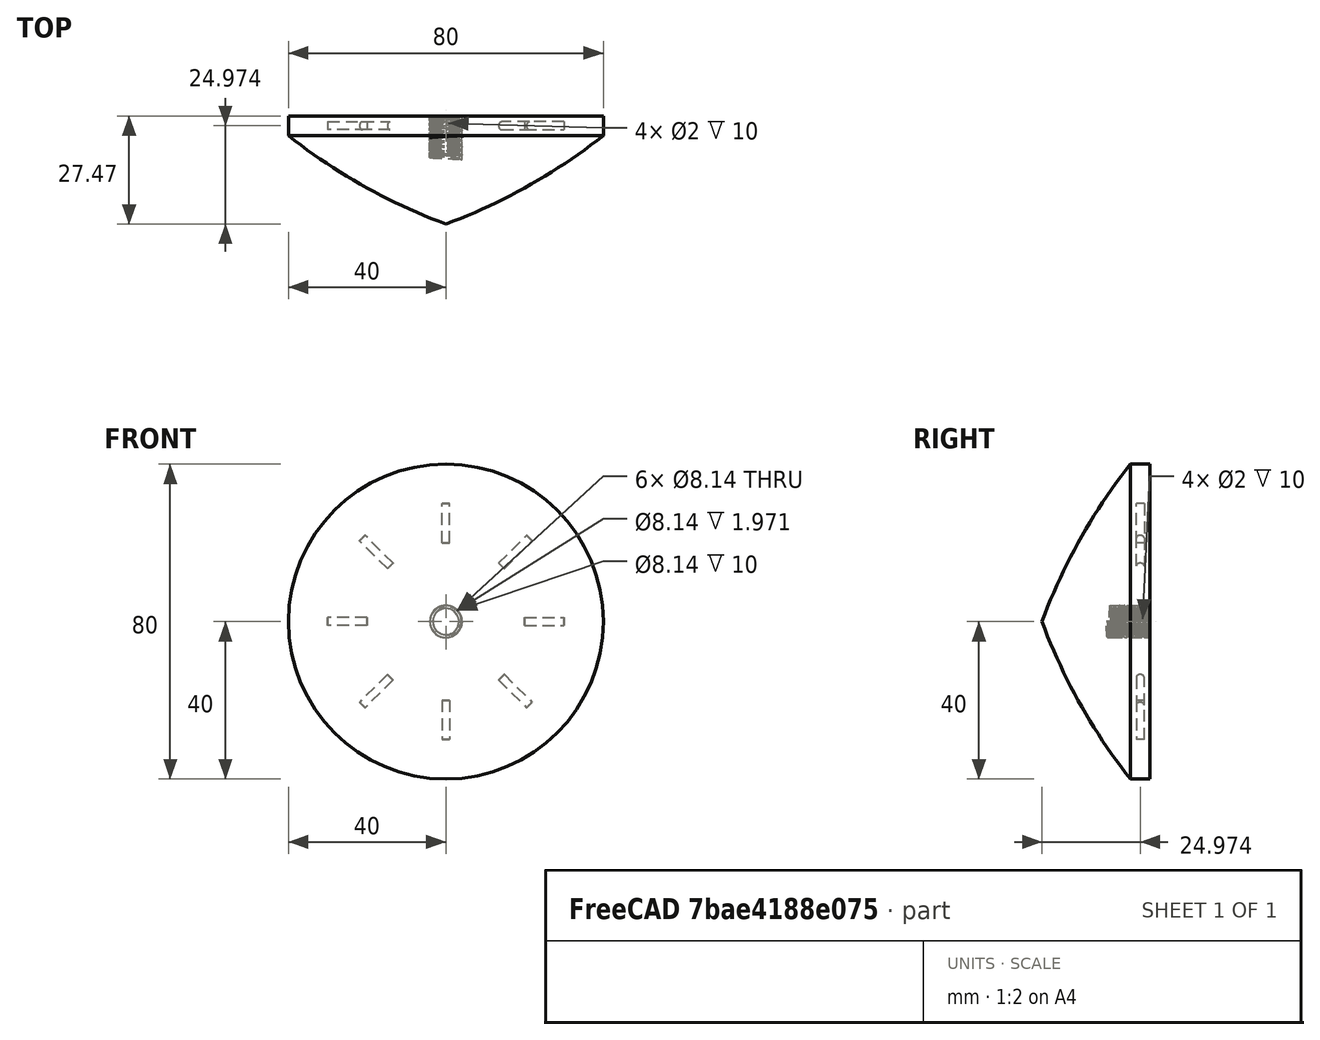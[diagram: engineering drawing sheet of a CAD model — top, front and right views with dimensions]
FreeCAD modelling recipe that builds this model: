
FCSTD DOCUMENT  (FreeCAD 0.19R24291 (Git))
Label: conefinal2filet
License: All rights reserved
LicenseURL: http://en.wikipedia.org/wiki/All_rights_reserved
objects: Sketcher::SketchObject×4, PartDesign::Body×2, PartDesign::Revolution×1, PartDesign::PolarPattern×1, PartDesign::Pocket×1, Part::Helix×1, Part::Sweep×1, Part::Fuse×1, PartDesign::FeatureBase×1, PartDesign::Groove×1, Mesh::Feature×1
note: 17 computed .brp shape members not serialized (recipe doc carries the construction recipe); baked Part::Feature solids carry a one-line shape summary decoded from their .brp

FEATURE [Sketcher::SketchObject] Sketch
  FullyConstrained = true
  MapMode = 5
  Support = -> [XY_Plane]
  sketch-geometry (8):
    g0: LineSegment StartX=0 StartY=-2.84e-14 StartZ=0 EndX=0 EndY=27.4735 EndZ=0
    g1: LineSegment StartX=0 StartY=27.4735 StartZ=0 EndX=40 EndY=27.4735 EndZ=0
    g2: LineSegment StartX=40 StartY=27.4735 StartZ=0 EndX=40 EndY=22.4735 EndZ=0
    g3: ArcOfEllipse CenterX=-50 CenterY=148.368 CenterZ=0 NormalX=0 NormalY=0 NormalZ=1 MajorRadius=157.368 MinorRadius=150 AngleXU=-1.5708 StartAngle=0.339837 EndAngle=0.643501
    g4: LineSegment StartX=-50 StartY=-9 StartZ=0 EndX=-50 EndY=305.735 EndZ=0
    g5: LineSegment StartX=100 StartY=148.368 StartZ=0 EndX=-200 EndY=148.368 EndZ=0
    g6: GeomPoint X=-50 Y=100.78 Z=0
    g7: GeomPoint X=-50 Y=195.955 Z=0
  constraints (15):
    c: Coincident(g0,g-1)
    c: PointOnObject(g0,g-2)
    c: Coincident(g1,g0)
    c: Horizontal(g1)
    c: Coincident(g2,g1)
    c: Vertical(g2)
    c: Distance(g1) = 40
    c: Distance(g2) = 5
    c: InternalAlignment(g4-g7 -> g3) x4
    c: Distance(g5) = 300
    c: Vertical(g4)
    c: DistanceX(g4,g0) = 50
    c: DistanceY(g4,g0) = 9
    c: Coincident(g3,g0)
    c: Coincident(g3,g2)
FEATURE [PartDesign::Revolution] Revolution
  Angle = 360
  Axis = (0,1,0)
  Base = (0,0,0)
  Profile = -> Sketch
  ReferenceAxis = -> Sketch [V_Axis]
  Reversed = true
FEATURE [PartDesign::PolarPattern] PolarPattern
  Angle = 360
  Axis = -> Y_Axis
  BaseFeature = -> Revolution
  Occurrences = 8
FEATURE [Sketcher::SketchObject] Sketch002
  FullyConstrained = true
  MapMode = 5
  Placement = pos=(0,27.4735,0) rot=(0,0.707107,0.707107;3.14159rad)
  Support = -> [PolarPattern]
  sketch-geometry (1):
    g0: Circle CenterX=0 CenterY=0 CenterZ=0 NormalX=0 NormalY=0 NormalZ=1 AngleXU=0 Radius=4.07
  constraints (2):
    c: Coincident(g0,g-1)
    c: Radius(g0) = 4.07
FEATURE [PartDesign::Pocket] Pocket001
  BaseFeature = -> PolarPattern
  Length = 10
  Length2 = 100
  Profile = -> Sketch002
  Type = 0
FEATURE [Part::Helix] Helix  label="Hélice"
  Angle = 0
  AttacherType = Attacher::AttachEngine3D
  Height = 11.25
  LocalCoord = 0
  MapMode = 2
  Pitch = 1.25
  Placement = pos=(0,26.25,0) rot=(1,0,0;1.5708rad)
  Radius = 3.33
  Style = 1
FEATURE [Sketcher::SketchObject] Sketch003
  FullyConstrained = true
  MapMode = 5
  Support = -> [XY_Plane]
  sketch-geometry (4):
    g0: LineSegment StartX=3.325 StartY=15.1346 StartZ=0 EndX=3.325 EndY=14.75 EndZ=0
    g1: LineSegment StartX=3.325 StartY=15.1346 StartZ=0 EndX=4.07 EndY=15.5648 EndZ=0
    g2: LineSegment StartX=3.325 StartY=14.75 StartZ=0 EndX=4.07 EndY=14.3199 EndZ=0
    g3: LineSegment StartX=4.07 StartY=15.5648 StartZ=0 EndX=4.07 EndY=14.3199 EndZ=0
  constraints (12):
    c: Vertical(g0)
    c: Coincident(g1,g0)
    c: Coincident(g2,g0)
    c: Coincident(g3,g1)
    c: Coincident(g3,g2)
    c: Vertical(g3)
    c: Equal(g2,g1)
    c: DistanceX(g-1,g0) = 3.325
    c: Angle(g2,g1) = 1.0472
    c: Distance(g3) = 1.2449
    c: DistanceX(g-1,g2) = 4.07
    c: DistanceY(g-1,g0) = 14.75
FEATURE [PartDesign::Body] Body
  Group = -> [Sketch,Revolution,PolarPattern,Sketch002,Pocket001,Sketch003]
  Origin = -> Origin
  Tip = -> Pocket001
FEATURE [Part::Sweep] Sweep
  Frenet = true
  Placement = pos=(0,2,0) rot=(0,0,1;0rad)
  Sections = -> [Sketch003]
  Solid = true
  Spine = -> Helix
  Transition = 1
FEATURE [Part::Fuse] Fusion
  Base = -> Pocket001
  Tool = -> Sweep
FEATURE [PartDesign::FeatureBase] BaseFeature
  BaseFeature = -> Fusion
FEATURE [Sketcher::SketchObject] Sketch004
  ExternalGeometry = -> [BaseFeature]
  FullyConstrained = true
  MapMode = 5
  Support = -> [XY_Plane001]
  sketch-geometry (4):
    g0: LineSegment StartX=-5 StartY=29.4735 StartZ=0 EndX=0 EndY=29.4735 EndZ=0
    g1: LineSegment StartX=0 StartY=29.4735 StartZ=0 EndX=0 EndY=27.4735 EndZ=0
    g2: LineSegment StartX=0 StartY=27.4735 StartZ=0 EndX=-5 EndY=27.4735 EndZ=0
    g3: LineSegment StartX=-5 StartY=27.4735 StartZ=0 EndX=-5 EndY=29.4735 EndZ=0
  constraints (12):
    c: Coincident(g0,g1)
    c: Coincident(g1,g2)
    c: Coincident(g2,g3)
    c: Coincident(g3,g0)
    c: Horizontal(g0)
    c: Horizontal(g2)
    c: Vertical(g1)
    c: Vertical(g3)
    c: PointOnObject(g1,g-2)
    c: PointOnObject(g2,g-3)
    c: Distance(g0) = 5
    c: Distance(g3) = 2
FEATURE [PartDesign::Groove] Groove
  Angle = 360
  Axis = (0,1,0)
  Base = (0,0,0)
  BaseFeature = -> BaseFeature
  Profile = -> Sketch004
  ReferenceAxis = -> Sketch004 [V_Axis]
  Reversed = true
FEATURE [PartDesign::Body] Body001
  BaseFeature = -> Fusion
  Group = -> [BaseFeature,Sketch004,Groove]
  Origin = -> Origin001
  Tip = -> Groove
FEATURE [Mesh::Feature] Mesh  label="Body001 (Meshed)"
